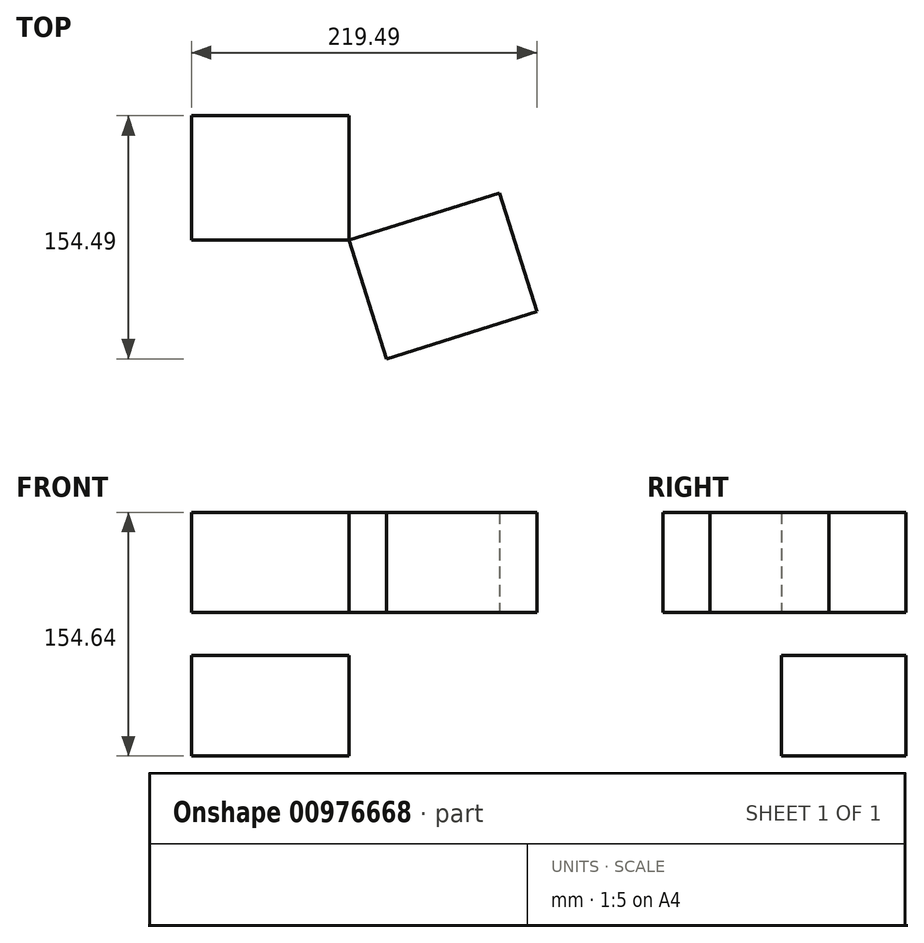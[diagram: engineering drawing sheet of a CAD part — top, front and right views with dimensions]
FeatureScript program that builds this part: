
annotation { "Feature Type Name" : "Feature", "Feature Type Description" : "" }
export const myFeature = defineFeature(function(context is Context, id is Id, definition is map)
    precondition{}
    {
        {
            var Q0;
            Q0=qCreatedBy(makeId("Top.planeOp"),FACE);
            var sketch = newSketch(context, id + "F0", { "sketchPlane" : qUnion([Q0])});
            skLineSegment(sketch, "E0.bottom", {"start": v(-45.82, 37.12) * mm, "end": v(54.4, 37.12) * mm});
            skLineSegment(sketch, "E0.top", {"start": v(-45.82, -41.93) * mm, "end": v(54.4, -41.93) * mm});
            skLineSegment(sketch, "E0.left", {"start": v(-45.82, 37.12) * mm, "end": v(-45.82, -41.93) * mm});
            skLineSegment(sketch, "E0.right", {"start": v(54.4, 37.12) * mm, "end": v(54.4, -41.93) * mm});
            skSolve(sketch);
        }
        {
            var Q0;
            Q0=makeQuery(id+"F0.imprint","IMPRINT",FACE,{"disambiguationData":[TD([[makeQuery(id+"F0.imprint","IMPRINT",EDGE,{"derivedFrom":sQuery(id+"F0.wireOp",EDGE,"E0.bottom")}),-1.0]])]});
            extrude(context, id + "F1", {"entities" : qUnion([Q0]), "depth" : 63.7 * mm, "offsetDistance" : 25.4 * mm});
        }
        {
            var Q0;
            Q0=makeQuery(id+"F1.opExtrude","SWEPT_BODY",BODY,{"disambiguationData":[OSD([sQuery(id+"F0.wireOp",EDGE,"E0.bottom"),sQuery(id+"F0.wireOp",EDGE,"E0.top"),sQuery(id+"F0.wireOp",EDGE,"E0.left"),sQuery(id+"F0.wireOp",EDGE,"E0.right")])]});
            transform(context, id + "F2", {"entities" : qUnion([Q0]), "transformType" : TransformType.COPY});
        }
        {
            var Q0;
            Q0=makeQuery(id+"F1.opExtrude","SWEPT_BODY",BODY,{"disambiguationData":[OSD([sQuery(id+"F0.wireOp",EDGE,"E0.bottom"),sQuery(id+"F0.wireOp",EDGE,"E0.top"),sQuery(id+"F0.wireOp",EDGE,"E0.left"),sQuery(id+"F0.wireOp",EDGE,"E0.right")])]});
            transform(context, id + "F3", {"entities" : qUnion([Q0]), "transformType" : TransformType.TRANSLATION_3D, "dx" : 0 * mm, "dy" : 0 * mm, "dz" : 90.93 * mm, "makeCopy" : false});
        }
        {
            var Q0;
            Q0=makeQuery(id+"F1.opExtrude","SWEPT_BODY",BODY,{"disambiguationData":[OSD([sQuery(id+"F0.wireOp",EDGE,"E0.bottom"),sQuery(id+"F0.wireOp",EDGE,"E0.top"),sQuery(id+"F0.wireOp",EDGE,"E0.left"),sQuery(id+"F0.wireOp",EDGE,"E0.right")])]});
            var Q1;
            Q1=makeQuery(id+"F2.opPattern","COPY",EDGE,{"derivedFrom":makeQuery(id+"F1.opExtrude","SWEPT_EDGE",EDGE,{"disambiguationData":[OSD([sQuery(id+"F0.wireOp",EDGE,"E0.top"),sQuery(id+"F0.wireOp",EDGE,"E0.right")])]}),"instanceName":"1"});
            transform(context, id + "F4", {"entities" : qUnion([Q0]), "transformType" : TransformType.ROTATION, "transformAxis" : qUnion([Q1]), "angle" : 162.62 * degree, "makeCopy" : true});
        }
    });
